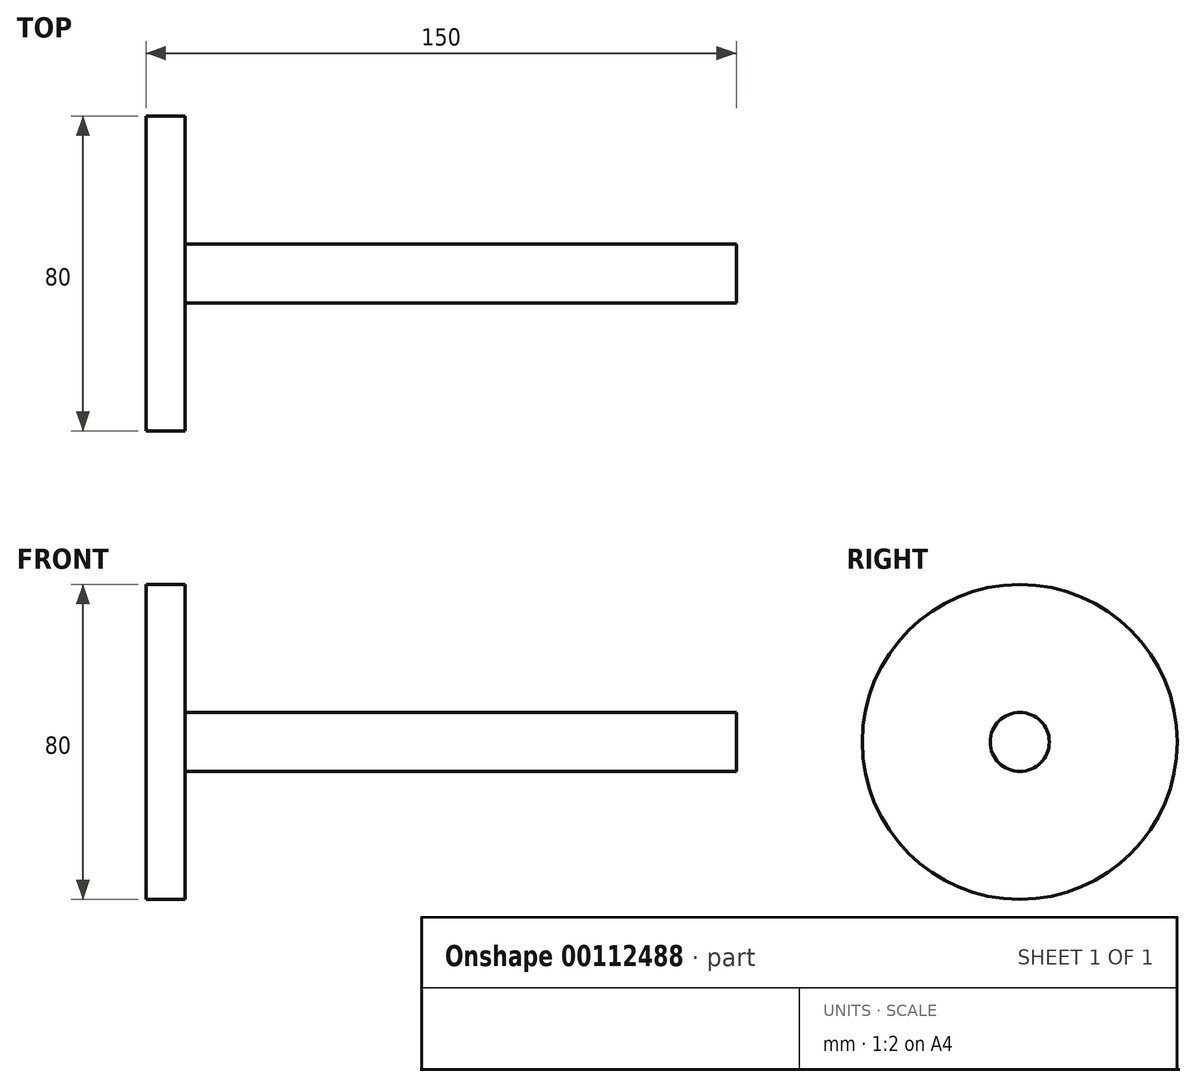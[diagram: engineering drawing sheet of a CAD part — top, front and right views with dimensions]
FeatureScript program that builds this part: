
annotation { "Feature Type Name" : "Feature", "Feature Type Description" : "" }
export const myFeature = defineFeature(function(context is Context, id is Id, definition is map)
    precondition{}
    {
        {
            var Q0;
            Q0=qCreatedBy(makeId("Front.planeOp"),FACE);
            var sketch = newSketch(context, id + "F0", { "sketchPlane" : qUnion([Q0])});
            skLineSegment(sketch, "E0.bottom", {"start": v(-4.27, 40) * mm, "end": v(5.73, 40) * mm});
            skLineSegment(sketch, "E0.left", {"start": v(-4.27, 40) * mm, "end": v(-4.27, 0) * mm});
            skLineSegment(sketch, "E0.right", {"start": v(5.73, 40) * mm, "end": v(5.73, 0) * mm});
            skPoint(sketch, "E0.middle", {"position": v(0, 0) * mm});
            skLineSegment(sketch, "E1.top", {"start": v(-4.27, 7.5) * mm, "end": v(145.73, 7.5) * mm});
            skLineSegment(sketch, "E1.right", {"start": v(145.73, 0) * mm, "end": v(145.73, 7.5) * mm});
            skPoint(sketch, "E1.middle", {"position": v(25.72, 0) * mm});
            skLineSegment(sketch, "E2", {"start": v(-49.32, 0) * mm, "end": v(196.31, 0) * mm});
            skSolve(sketch);
        }
        {
            var Q0;
            Q0 = qSketchRegion(id + "F0", true);
            var Q1;
            Q1=sQuery(id+"F0.wireOp",EDGE,"E2");
            revolve(context, id + "F1", {"entities" : qUnion([Q0]), "axis" : qUnion([Q1]), "revolveType" : RevolveType.FULL});
        }
    });
